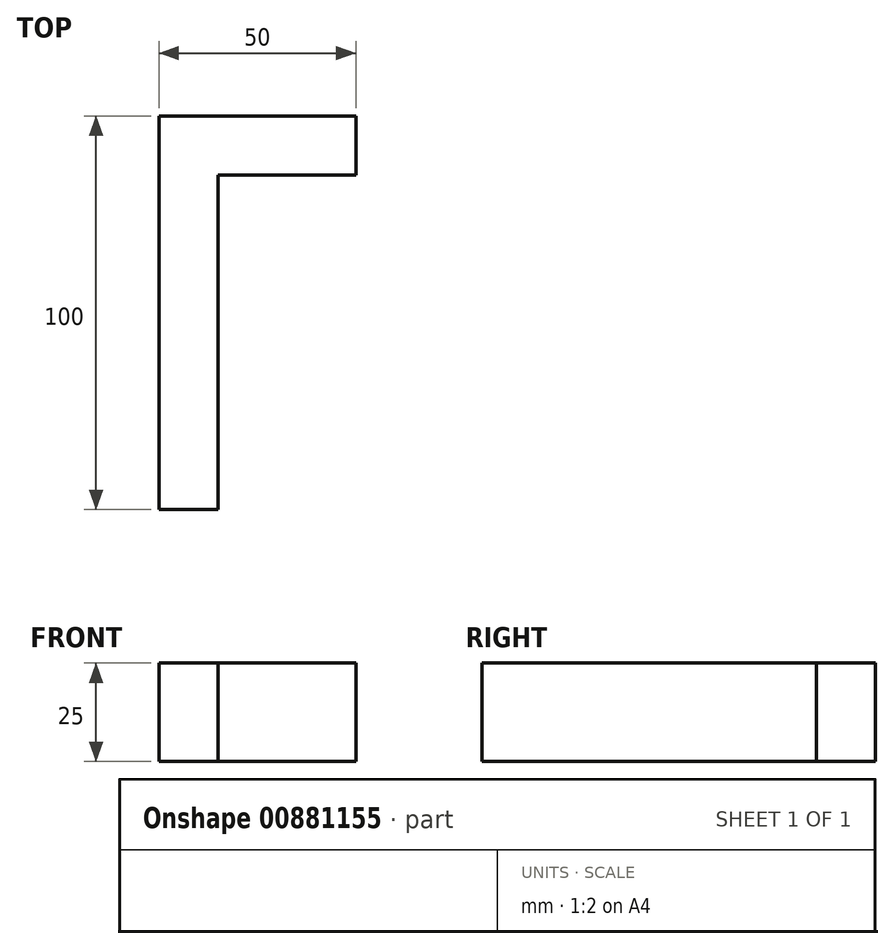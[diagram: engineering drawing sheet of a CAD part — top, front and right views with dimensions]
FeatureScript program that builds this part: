
annotation { "Feature Type Name" : "Feature", "Feature Type Description" : "" }
export const myFeature = defineFeature(function(context is Context, id is Id, definition is map)
    precondition{}
    {
        {
            var Q0;
            Q0=qCreatedBy(makeId("Top.planeOp"),FACE);
            var sketch = newSketch(context, id + "F0", { "sketchPlane" : qUnion([Q0])});
            skLineSegment(sketch, "E0.bottom", {"start": v(-64.16, 39.16) * mm, "end": v(-49.16, 39.16) * mm});
            skLineSegment(sketch, "E0.top", {"start": v(-64.16, -60.84) * mm, "end": v(-49.16, -60.84) * mm});
            skLineSegment(sketch, "E0.left", {"start": v(-64.16, 39.16) * mm, "end": v(-64.16, -60.84) * mm});
            skLineSegment(sketch, "E0.right", {"start": v(-49.16, 39.16) * mm, "end": v(-49.16, -60.84) * mm});
            skLineSegment(sketch, "E1.bottom", {"start": v(-49.16, 39.16) * mm, "end": v(-14.16, 39.16) * mm});
            skLineSegment(sketch, "E1.top", {"start": v(-49.16, 24.16) * mm, "end": v(-14.16, 24.16) * mm});
            skLineSegment(sketch, "E1.left", {"start": v(-49.16, 39.16) * mm, "end": v(-49.16, 24.16) * mm});
            skLineSegment(sketch, "E1.right", {"start": v(-14.16, 39.16) * mm, "end": v(-14.16, 24.16) * mm});
            skSolve(sketch);
        }
        {
            var Q0;
            {var subQ3=sQuery(id+"F0.wireOp",EDGE,"E0.bottom");Q0=makeQuery(id+"F0.imprint","IMPRINT",FACE,{"disambiguationData":[TD([[makeQuery(id+"F0.imprint","IMPRINT",EDGE,{"derivedFrom":subQ3}),-1.0]])]});}
            var Q1;
            {var subQ0=sQuery(id+"F0.wireOp",EDGE,"E1.bottom");Q1=makeQuery(id+"F0.imprint","IMPRINT",FACE,{"disambiguationData":[TD([[makeQuery(id+"F0.imprint","IMPRINT",EDGE,{"derivedFrom":subQ0}),-1.0]])]});}
            extrude(context, id + "F1", {"entities" : qUnion([Q0, Q1]), "depth" : 25 * mm, "offsetDistance" : 25 * mm});
        }
    });
